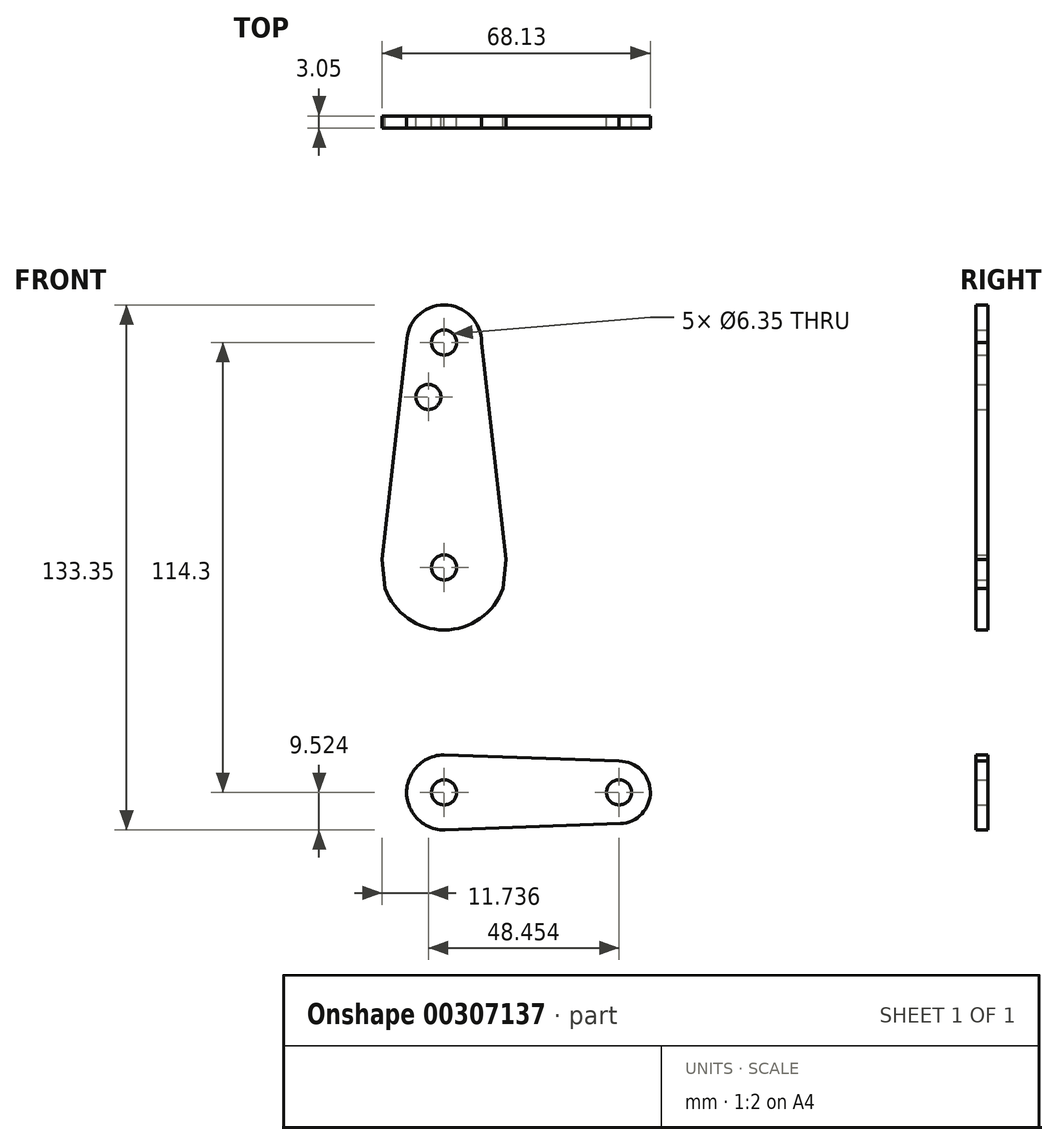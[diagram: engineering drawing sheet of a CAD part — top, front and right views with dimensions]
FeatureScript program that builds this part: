
annotation { "Feature Type Name" : "Feature", "Feature Type Description" : "" }
export const myFeature = defineFeature(function(context is Context, id is Id, definition is map)
    precondition{}
    {
        {
            var Q0;
            Q0=qCreatedBy(makeId("Front.planeOp"),FACE);
            var sketch = newSketch(context, id + "F0", { "sketchPlane" : qUnion([Q0])});
            skLineSegment(sketch, "E0", {"start": v(-31.57, 55.07) * mm, "end": v(-31.57, -59.23) * mm, "construction": true});
            skLineSegment(sketch, "E1", {"start": v(-31.57, -59.23) * mm, "end": v(12.88, -59.23) * mm, "construction": true});
            skCircle(sketch, "E2", {"center": v(12.88, -59.23) * mm, "radius": 7.94 * mm});
            skCircle(sketch, "E3", {"center": v(-31.57, -59.23) * mm, "radius": 9.53 * mm});
            skCircle(sketch, "E4", {"center": v(-31.57, 55.07) * mm, "radius": 9.53 * mm});
            skCircle(sketch, "E5", {"center": v(-31.57, -2.08) * mm, "radius": 15.88 * mm});
            skLineSegment(sketch, "E6", {"start": v(-41.1, 55.07) * mm, "end": v(-47.31, 0) * mm});
            skLineSegment(sketch, "E7", {"start": v(-22.04, 55.07) * mm, "end": v(-15.83, 0) * mm});
            skLineSegment(sketch, "E8", {"start": v(-47.31, 0) * mm, "end": v(-41.1, -59.23) * mm});
            skLineSegment(sketch, "E9", {"start": v(-15.83, 0) * mm, "end": v(-22.04, -59.23) * mm});
            skLineSegment(sketch, "E10", {"start": v(-31.57, -49.7) * mm, "end": v(12.88, -51.29) * mm});
            skCircle(sketch, "E11", {"center": v(-31.57, 55.07) * mm, "radius": 3.18 * mm});
            skCircle(sketch, "E12", {"center": v(-31.57, -2.08) * mm, "radius": 3.18 * mm});
            skCircle(sketch, "E13", {"center": v(-31.57, -59.23) * mm, "radius": 3.18 * mm});
            skCircle(sketch, "E14", {"center": v(12.88, -59.23) * mm, "radius": 3.18 * mm});
            skCircle(sketch, "E15", {"center": v(-35.57, 41.26) * mm, "radius": 3.18 * mm});
            skLineSegment(sketch, "E16", {"start": v(-31.3, -68.75) * mm, "end": v(13.16, -67.16) * mm});
            skSolve(sketch);
        }
        {
            var Q0;
            {var subQ0=sQuery(id+"F0.wireOp",EDGE,"E16");var subQ1=sQuery(id+"F0.wireOp",EDGE,"E3");var subQ2=makeQuery(id+"F0.imprint","INTERSECT",VERTEX,{"disambiguationData":[OD(0.0)],"derivedFrom":[subQ1,subQ0]});Q0=makeQuery(id+"F0.imprint","IMPRINT",FACE,{"disambiguationData":[TD([[makeQuery(id+"F0.imprint","IMPRINT",EDGE,{"disambiguationData":[TD([[subQ2,-1.0]])],"derivedFrom":subQ1}),1.0]])]});}
            var Q1;
            {var subQ0=sQuery(id+"F0.wireOp",EDGE,"E8");var subQ1=sQuery(id+"F0.wireOp",EDGE,"E5");var subQ2=makeQuery(id+"F0.imprint","INTERSECT",VERTEX,{"disambiguationData":[OD(0.0)],"derivedFrom":[subQ1,subQ0]});Q1=makeQuery(id+"F0.imprint","IMPRINT",FACE,{"disambiguationData":[TD([[makeQuery(id+"F0.imprint","IMPRINT",EDGE,{"disambiguationData":[TD([[subQ2,-1.0]])],"derivedFrom":subQ1}),1.0]])]});}
            var Q2;
            {var subQ0=sQuery(id+"F0.wireOp",EDGE,"E9");var subQ1=sQuery(id+"F0.wireOp",EDGE,"E5");var subQ2=makeQuery(id+"F0.imprint","INTERSECT",VERTEX,{"disambiguationData":[OD(0.0)],"derivedFrom":[subQ1,subQ0]});Q2=makeQuery(id+"F0.imprint","IMPRINT",FACE,{"disambiguationData":[TD([[makeQuery(id+"F0.imprint","IMPRINT",EDGE,{"disambiguationData":[TD([[subQ2,1.0]])],"derivedFrom":subQ1}),1.0]])]});}
            var Q3;
            Q3=makeQuery(id+"F0.imprint","IMPRINT",FACE,{"disambiguationData":[TD([[makeQuery(id+"F0.imprint","IMPRINT",EDGE,{"derivedFrom":sQuery(id+"F0.wireOp",EDGE,"E14")}),-1.0]])]});
            var Q4;
            Q4=makeQuery(id+"F0.imprint","IMPRINT",FACE,{"disambiguationData":[TD([[makeQuery(id+"F0.imprint","IMPRINT",EDGE,{"derivedFrom":sQuery(id+"F0.wireOp",EDGE,"E11")}),-1.0]])]});
            var Q5;
            {var subQ3=sQuery(id+"F0.wireOp",EDGE,"E10");var subQ5=sQuery(id+"F0.wireOp",EDGE,"E2");var subQ6=makeQuery(id+"F0.imprint","INTERSECT",VERTEX,{"derivedFrom":[subQ5,subQ3]});Q5=makeQuery(id+"F0.imprint","IMPRINT",FACE,{"disambiguationData":[TD([[makeQuery(id+"F0.imprint","IMPRINT",EDGE,{"disambiguationData":[TD([[subQ6,-1.0]])],"derivedFrom":subQ5}),-1.0]])]});}
            var Q6;
            {var subQ0=sQuery(id+"F0.wireOp",EDGE,"E9");var subQ1=sQuery(id+"F0.wireOp",EDGE,"E3");var subQ2=makeQuery(id+"F0.imprint","INTERSECT",VERTEX,{"derivedFrom":[subQ1,subQ0]});Q6=makeQuery(id+"F0.imprint","IMPRINT",FACE,{"disambiguationData":[TD([[makeQuery(id+"F0.imprint","IMPRINT",EDGE,{"disambiguationData":[TD([[subQ2,-1.0]])],"derivedFrom":subQ1}),-1.0]])]});}
            var Q7;
            {var subQ5=sQuery(id+"F0.wireOp",EDGE,"E3");var subQ7=sQuery(id+"F0.wireOp",EDGE,"E10");var subQ8=makeQuery(id+"F0.imprint","INTERSECT",VERTEX,{"disambiguationData":[OD(0.0)],"derivedFrom":[subQ5,subQ7]});Q7=makeQuery(id+"F0.imprint","IMPRINT",FACE,{"disambiguationData":[TD([[makeQuery(id+"F0.imprint","IMPRINT",EDGE,{"disambiguationData":[TD([[subQ8,1.0]])],"derivedFrom":subQ5}),-1.0]])]});}
            var Q8;
            Q8=makeQuery(id+"F0.imprint","IMPRINT",FACE,{"disambiguationData":[TD([[makeQuery(id+"F0.imprint","IMPRINT",EDGE,{"derivedFrom":sQuery(id+"F0.wireOp",EDGE,"E12")}),-1.0]])]});
            var Q9;
            Q9=makeQuery(id+"F0.imprint","IMPRINT",FACE,{"disambiguationData":[TD([[makeQuery(id+"F0.imprint","IMPRINT",EDGE,{"derivedFrom":sQuery(id+"F0.wireOp",EDGE,"E13")}),-1.0]])]});
            var Q10;
            {var subQ6=sQuery(id+"F0.wireOp",EDGE,"E6");Q10=makeQuery(id+"F0.imprint","IMPRINT",FACE,{"disambiguationData":[TD([[makeQuery(id+"F0.imprint","IMPRINT",EDGE,{"derivedFrom":subQ6}),1.0]])]});}
            extrude(context, id + "F1", {"entities" : qUnion([Q0, Q1, Q2, Q3, Q4, Q5, Q6, Q7, Q8, Q9, Q10]), "depth" : 3.05 * mm});
        }
    });
